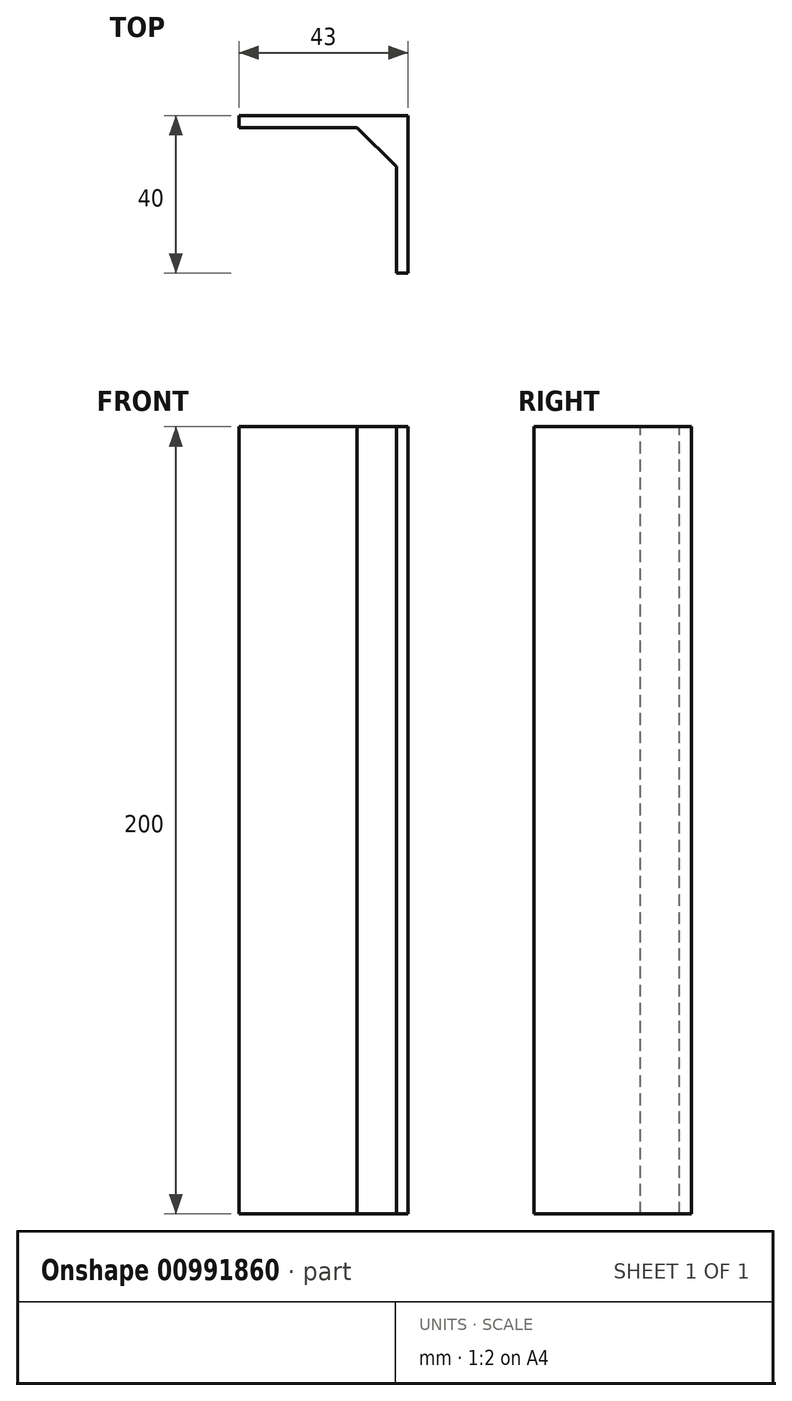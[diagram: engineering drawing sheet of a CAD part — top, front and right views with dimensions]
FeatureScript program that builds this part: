
annotation { "Feature Type Name" : "Feature", "Feature Type Description" : "" }
export const myFeature = defineFeature(function(context is Context, id is Id, definition is map)
    precondition{}
    {
        {
            var Q0;
            Q0=qCreatedBy(makeId("Front.planeOp"),FACE);
            var sketch = newSketch(context, id + "F0", { "sketchPlane" : qUnion([Q0])});
            skLineSegment(sketch, "E0.bottom", {"start": v(20, -100) * mm, "end": v(-20, -100) * mm});
            skLineSegment(sketch, "E0.top", {"start": v(20, 100) * mm, "end": v(-20, 100) * mm});
            skLineSegment(sketch, "E0.left", {"start": v(20, -100) * mm, "end": v(20, 100) * mm});
            skLineSegment(sketch, "E0.right", {"start": v(-20, -100) * mm, "end": v(-20, 100) * mm});
            skPoint(sketch, "E0.middle", {"position": v(0, 0) * mm});
            skSolve(sketch);
        }
        {
            var Q0;
            Q0 = qSketchRegion(id + "F0", true);
            extrude(context, id + "F1", {"entities" : qUnion([Q0]), "depth" : 3 * mm, "offsetDistance" : 25 * mm});
        }
        {
            var Q0;
            Q0=qCreatedBy(makeId("Front.planeOp"),FACE);
            var sketch = newSketch(context, id + "F2", { "sketchPlane" : qUnion([Q0])});
            skLineSegment(sketch, "E1.bottom", {"start": v(23, -100) * mm, "end": v(20, -100) * mm});
            skLineSegment(sketch, "E1.top", {"start": v(23, 100) * mm, "end": v(20, 100) * mm});
            skLineSegment(sketch, "E1.left", {"start": v(23, -100) * mm, "end": v(23, 100) * mm});
            skLineSegment(sketch, "E1.right", {"start": v(20, -100) * mm, "end": v(20, 100) * mm});
            skPoint(sketch, "E1.middle", {"position": v(21.5, 0) * mm});
            skSolve(sketch);
        }
        {
            var Q0;
            Q0 = qSketchRegion(id + "F2", true);
            extrude(context, id + "F3", {"entities" : qUnion([Q0]), "operationType" : NewBodyOperationType.ADD, "depth" : 40 * mm, "offsetDistance" : 25 * mm});
        }
        {
            var Q0;
            Q0=qCreatedBy(makeId("Top.planeOp"),FACE);
            var sketch = newSketch(context, id + "F4", { "sketchPlane" : qUnion([Q0])});
            skLineSegment(sketch, "E2", {"start": v(20, -13) * mm, "end": v(10, -3) * mm});
            skLineSegment(sketch, "E3", {"start": v(20, -13) * mm, "end": v(20, -3) * mm});
            skLineSegment(sketch, "E4", {"start": v(20, -3) * mm, "end": v(10, -3) * mm});
            skSolve(sketch);
        }
        {
            var Q0;
            Q0=makeQuery(id+"F4.imprint","IMPRINT",FACE,{"disambiguationData":[TD([[makeQuery(id+"F4.imprint","IMPRINT",EDGE,{"derivedFrom":sQuery(id+"F4.wireOp",EDGE,"E2")}),-1.0]])]});
            extrude(context, id + "F5", {"entities" : qUnion([Q0]), "operationType" : NewBodyOperationType.ADD, "oppositeDirection" : true, "depth" : 200 * mm, "offsetDistance" : 25 * mm, "symmetric" : true});
        }
    });
